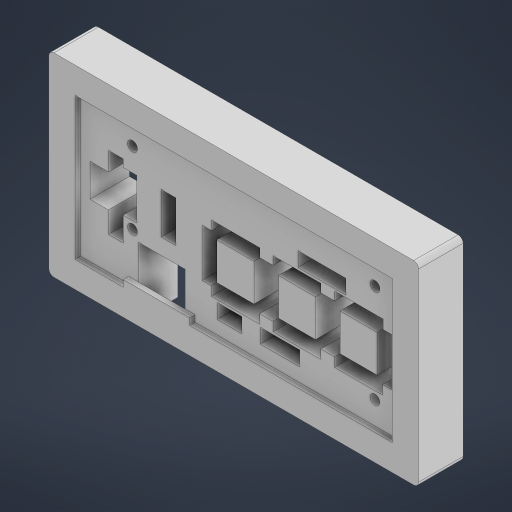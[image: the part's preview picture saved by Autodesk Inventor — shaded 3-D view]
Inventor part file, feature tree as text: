
AUTODESK INVENTOR PART (.ipt)
format: ipt  version: 2024.1 (Build 281209000, 209)  size: 5,022,720 bytes
history: native  units: mm
features: projected_geometry x7, extrude x5, sketch x5, other x2, plane x1, fillet x1
ambient origin geometry x8: Origin, YZ Plane, XZ Plane, XY Plane, X Axis, Y Axis, Z Axis, Center Point
bodies: Solid1 (feature_tree)
feature tree (21):
  other  "3D_PCB1_2024-08-12"
  extrude  "Extrusion1"  Depth=10.0mm
  sketch  "Sketch2"  dims[d2=2.0mm d3=2.0mm]
  plane  "Work Plane1"
  extrude  "Extrusion2"  Depth=2.0mm
  extrude  "Extrusion3"  Depth=1.0mm
  extrude  "Extrusion4"  Depth=1.0mm
  fillet  "Fillet1"  Radius=1.0mm
  extrude  "Extrusion5"  Depth=10.0mm
  sketch  "Sketch1"  dims[d0=2.0mm d1=10.0mm]
  sketch  "Sketch3"  dims[d4=2.5mm d5=1.0mm]
  sketch  "Sketch4"  dims[d6=1.0mm d7=1.0mm d10=1.0mm]
  sketch  "Sketch5"  dims[d11=1.0mm d12=1.0mm d13=1.0mm d14=1.0mm d15=1.0mm d16=1.0mm d17=1.0mm d18=1.0mm d19=1.0mm d20=1.0mm d21=1.0mm d22=1.0mm d23=1.0mm d24=1.0mm d25=1.0mm d26=1.0mm d27=1.0mm d28=1.0mm d29=1.0mm d30=1.0mm d31=1.0mm d32=1.0mm d33=1.0mm d34=1.0mm d35=1.0mm d36=1.0mm d37=1.0mm d38=1.0mm d39=1.0mm d40=1.0mm d41=1.0mm d42=1.0mm d43=1.0mm d44=1.0mm d45=1.0mm d46=1.0mm d47=1.0mm d48=1.0mm d49=1.0mm d50=1.0mm d51=1.0mm d52=1.0mm d53=1.0mm d54=1.0mm d55=1.0mm d56=1.0mm d57=1.0mm d58=1.0mm d59=1.0mm d60=1.0mm d61=1.0mm d62=1.0mm d63=1.0mm d64=1.0mm d65=1.0mm d66=1.0mm d67=3.0mm d68=3.0mm d69=3.0mm d70=3.0mm d71=10.0mm d72=0.0mm d73=2.0mm d74=0.0mm d75=10.0mm d76=0.0mm d77=3.0mm d78=3.0mm d79=10.0mm d80=0.0mm d81=7.853982mm d82=1.5mm d83=3.0mm d85=1.590604mm d86=1.590604mm d87=2.0mm d88=0.0mm d89=135.0deg d90=1.590604mm d91=18.796039mm d92=30.0mm d94=18.796039mm d95=10.0mm d97=10.0mm d99=1.5mm d100=10.0mm d101=0.0mm]
  projected_geometry  "Projected Loop1"
  projected_geometry  "Projected Loop2"
  projected_geometry  "Projected Loop3"
  projected_geometry  "Projected Loop4"
  projected_geometry  "Projected Loop5"
  projected_geometry  "Projected Loop6"
  projected_geometry  "Projected Loop7"
  other  "3D_PCB1_2024-08-12.obj"
